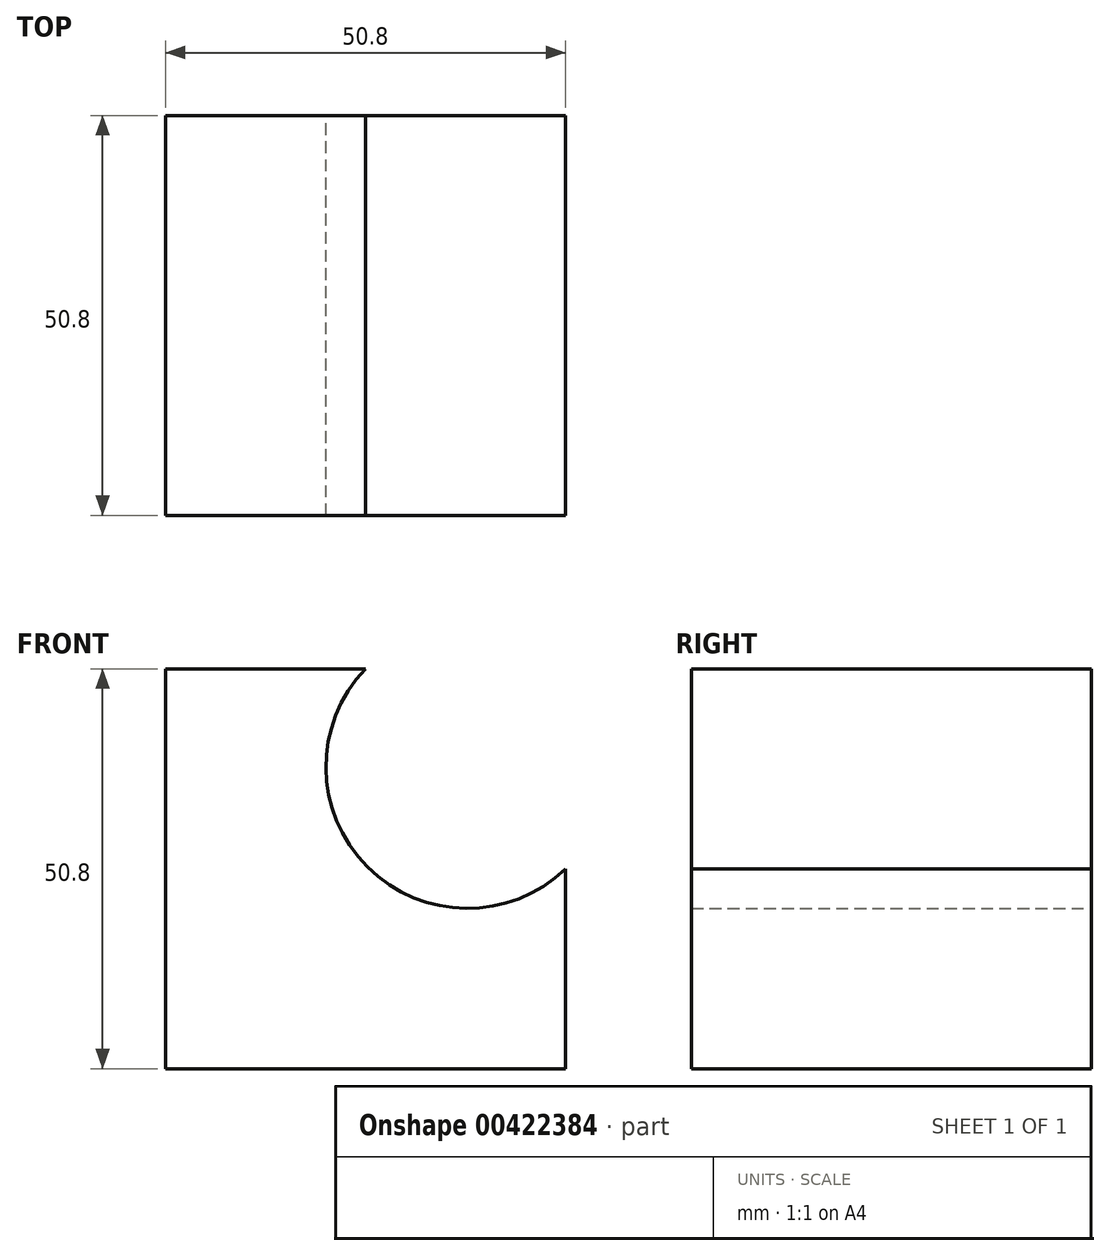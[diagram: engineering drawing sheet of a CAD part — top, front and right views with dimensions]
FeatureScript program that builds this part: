
annotation { "Feature Type Name" : "Feature", "Feature Type Description" : "" }
export const myFeature = defineFeature(function(context is Context, id is Id, definition is map)
    precondition{}
    {
        {
            var Q0;
            Q0=qCreatedBy(makeId("Front.planeOp"),FACE);
            var sketch = newSketch(context, id + "F0", { "sketchPlane" : qUnion([Q0])});
            skLineSegment(sketch, "E0", {"start": v(-28, 16.54) * mm, "end": v(-53.4, 16.54) * mm});
            skLineSegment(sketch, "E1", {"start": v(-53.4, 16.54) * mm, "end": v(-53.4, -34.26) * mm});
            skLineSegment(sketch, "E2", {"start": v(-53.4, -34.26) * mm, "end": v(-2.6, -34.26) * mm});
            skLineSegment(sketch, "E3", {"start": v(-2.6, -34.26) * mm, "end": v(-2.6, -8.86) * mm});
            skArc(sketch, "E4", {"start": v(-28, 16.54) * mm, "mid": v(-27.77, -8.63) * mm, "end": v(-2.6, -8.86) * mm});
            skSolve(sketch);
        }
        {
            var Q0;
            Q0=makeQuery(id+"F0.imprint","IMPRINT",FACE,{"disambiguationData":[TD([[makeQuery(id+"F0.imprint","IMPRINT",EDGE,{"derivedFrom":sQuery(id+"F0.wireOp",EDGE,"E0")}),1.0]])]});
            extrude(context, id + "F1", {"entities" : qUnion([Q0]), "depth" : 50.8 * mm});
        }
    });
